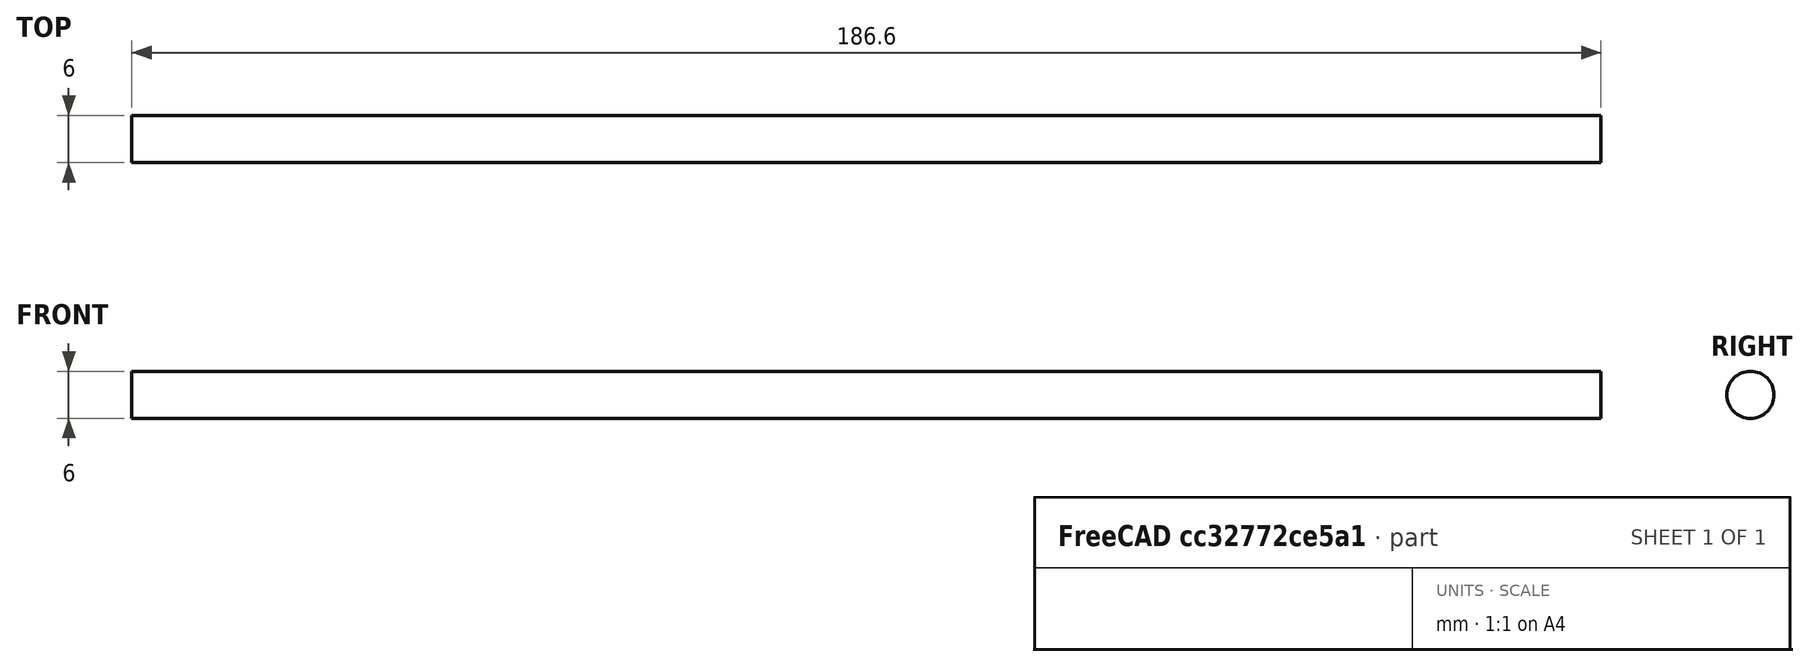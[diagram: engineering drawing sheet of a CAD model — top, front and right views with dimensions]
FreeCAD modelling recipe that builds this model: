
FCSTD DOCUMENT  (FreeCAD 0.19R18044 (Git))
Label: middle-stage-actuator-rod
License: Public Domain
LicenseURL: http://en.wikipedia.org/wiki/Public_domain
objects: Part::FeaturePython×6, App::FeaturePython×2, Sketcher::SketchObject×1, PartDesign::Pad×1, PartDesign::Body×1
note: 9 computed .brp shape members not serialized (recipe doc carries the construction recipe); baked Part::Feature solids carry a one-line shape summary decoded from their .brp

FEATURE [App::FeaturePython] Constraints  # WARN: FeaturePython — macro-defined, semantics opaque (R4)
  GroupMode = 1
  _Version = 1
FEATURE [Sketcher::SketchObject] Sketch
  MapMode = 5
  Placement = pos=(0,0,0) rot=(0.57735,0.57735,0.57735;2.0944rad)
  Support = -> [YZ_Plane]
  sketch-geometry (1):
    g0: Circle CenterX=0 CenterY=0 CenterZ=0 NormalX=0 NormalY=0 NormalZ=1 AngleXU=0 Radius=3
  constraints (2):
    c: Coincident(g0,g-1)
    c: Radius(g0) = 3
FEATURE [PartDesign::Pad] Pad
  ClaimChildren = false
  Length = 186.6
  Length2 = 100
  Midplane = true
  Placement = pos=(0,0,0) rot=(0.57735,0.57735,0.57735;2.0944rad)
  Profile = -> Sketch
  Type = 0
FEATURE [PartDesign::Body] Body
  Group = -> [Sketch,Pad]
  Origin = -> Origin
  Tip = -> Pad
FEATURE [Part::FeaturePython] Parts  # WARN: FeaturePython — macro-defined, semantics opaque (R4)
  Group = -> [Origin001,Body]
  GroupMode = 0
FEATURE [Part::FeaturePython] Element  label="center"  # link proxy (typed FeaturePython)
  Detach = false
  LinkTransform = true
  LinkedObject = -> Body [Pad.Sketch.Edge1]
  _Parent = -> Elements
FEATURE [Part::FeaturePython] Element001  label="left"  # link proxy (typed FeaturePython)
  Detach = false
  LinkTransform = true
  LinkedObject = -> Body [Pad.Edge2]
  _Parent = -> Elements
FEATURE [Part::FeaturePython] Element002  label="right"  # link proxy (typed FeaturePython)
  Detach = false
  LinkTransform = true
  LinkedObject = -> Body [Pad.Edge3]
  _Parent = -> Elements
FEATURE [App::FeaturePython] Elements  # WARN: FeaturePython — macro-defined, semantics opaque (R4)
  Group = -> [Element,Element001,Element002,Element003]
  GroupMode = 1
FEATURE [Part::FeaturePython] Assembly  label="middle-stage-actuator-rod"  # WARN: FeaturePython — macro-defined, semantics opaque (R4)
  AutoRelax = true
  BuildShape = 0
  Freeze = false
  Group = -> [Constraints,Elements,Parts]
  GroupMode = 1
  SolverType = 1
  Verbose = false
  _SolverType = 1
  _Version = 1
FEATURE [Part::FeaturePython] Element003  # link proxy (typed FeaturePython)
  Detach = false
  LinkTransform = true
  LinkedObject = -> Body [Pad.Face1]
  _Parent = -> Elements
